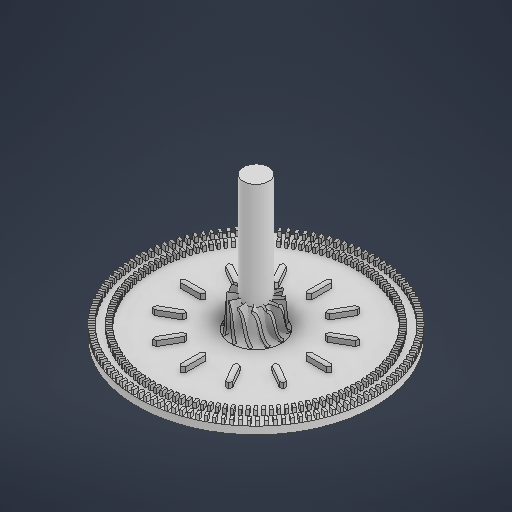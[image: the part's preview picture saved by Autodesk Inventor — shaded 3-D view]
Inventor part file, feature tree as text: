
AUTODESK INVENTOR PART (.ipt)
format: ipt  version: 2025 (Build 290162000, 162)  size: 5,212,160 bytes
history: native  units: mm
features: sketch x10, other x8, extrude x3, pattern_circular x3, revolve x1, projected_geometry x1
ambient origin geometry x8: Origin, YZ Plane, XZ Plane, XY Plane, X Axis, Y Axis, Z Axis, Center Point
bodies: Body1 (feature_tree), Body2 (feature_tree), Body3 (feature_tree)
feature tree (26):
  other  "Твердое тело1"
  revolve  "Вращение1"
  extrude  "Выдавливание1"  Depth=1.5mm
  pattern_circular  "Круговой массив1"  Angle=360.0deg  [1 undecoded]
  other  "РабПлоскость5"
  sketch  "Эскиз8"
  other  "РабПлоскость6"
  sketch  "Эскиз9"
  other  "РабПлоскость7"
  other  "Толщина1"
  pattern_circular  "Круговой массив2"  [2 undecoded]
  sketch  "Эскиз12"
  sketch  "Эскиз13"
  extrude  "Выдавливание3"  Depth=0.5mm
  pattern_circular  "Круговой массив3"  [2 undecoded]
  extrude  "Выдавливание4"  Depth=1200.0mm TaperAngle=360.0deg
  sketch  "Эскиз1"
  sketch  "Эскиз2"
  projected_geometry  "Спроецированная петля2"
  sketch  "Эскиз10"
  sketch  "Эскиз11"
  other  "SRF1"
  other  "Твердое тело2"
  sketch  "Эскиз15"
  sketch  "Эскиз16"
  other  "ПврхСеч1"
note: 5 required parameter values undecoded (feature->parameter linkage not recoverable at this tier; creation-order binding heuristic only, values carry confidence <= 0.55)
